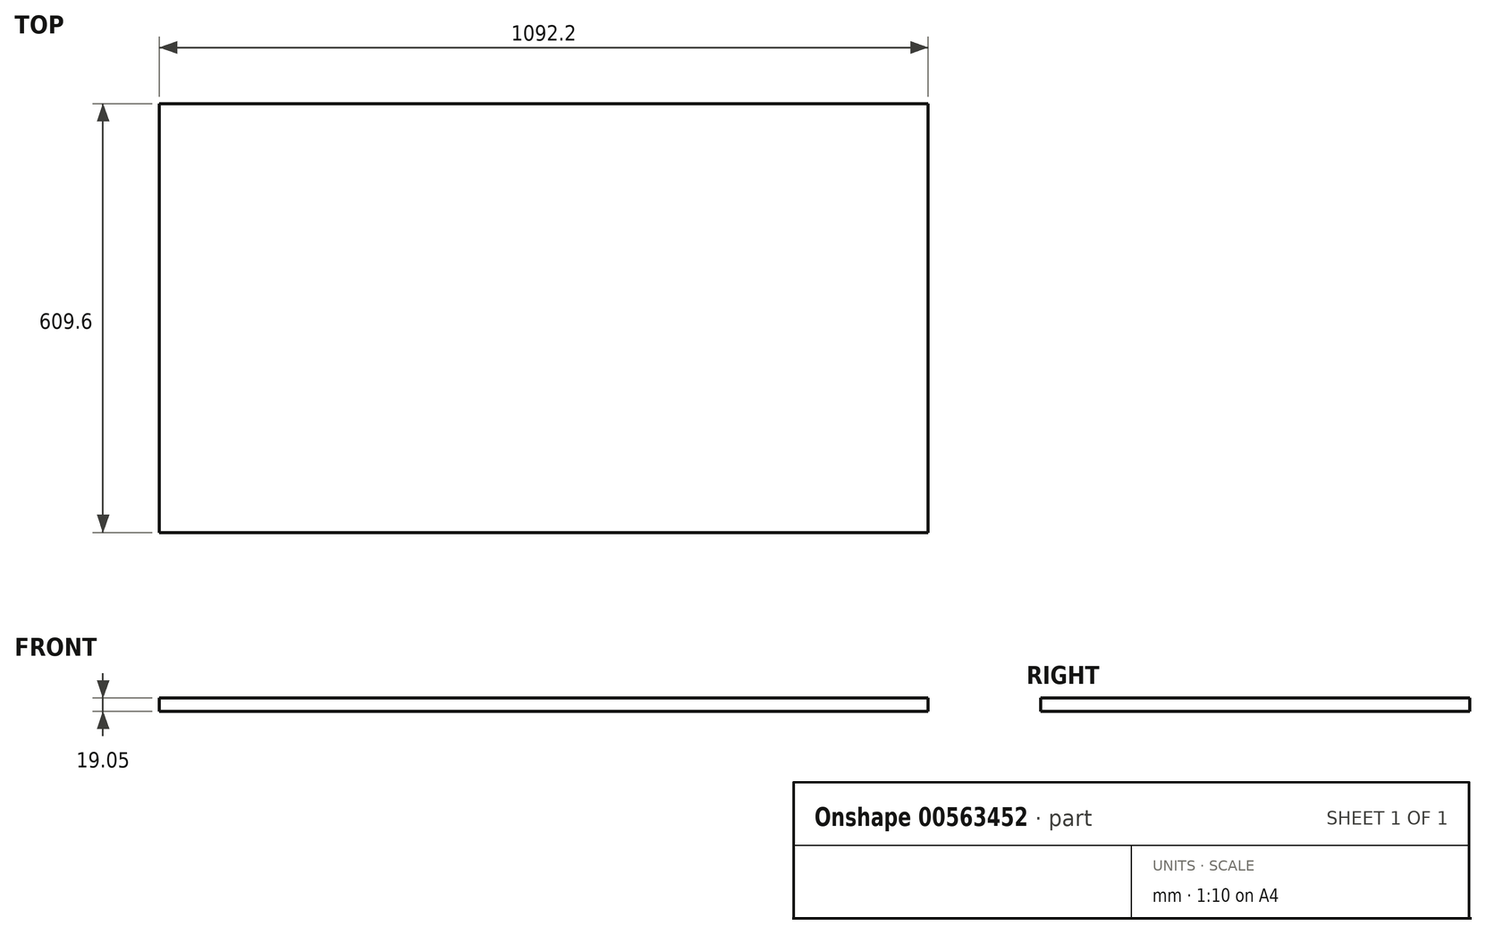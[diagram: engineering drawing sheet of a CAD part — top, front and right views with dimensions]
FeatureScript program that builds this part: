
annotation { "Feature Type Name" : "Feature", "Feature Type Description" : "" }
export const myFeature = defineFeature(function(context is Context, id is Id, definition is map)
    precondition{}
    {
        {
            var Q0;
            Q0=qCreatedBy(makeId("Top.planeOp"),FACE);
            var sketch = newSketch(context, id + "F0", { "sketchPlane" : qUnion([Q0])});
            skLineSegment(sketch, "E0.bottom", {"start": v(-265.33, 488.07) * mm, "end": v(826.87, 488.07) * mm});
            skLineSegment(sketch, "E0.top", {"start": v(-265.33, -121.53) * mm, "end": v(826.87, -121.53) * mm});
            skLineSegment(sketch, "E0.left", {"start": v(-265.33, 488.07) * mm, "end": v(-265.33, -121.53) * mm});
            skLineSegment(sketch, "E0.right", {"start": v(826.87, 488.07) * mm, "end": v(826.87, -121.53) * mm});
            skSolve(sketch);
        }
        {
            var Q0;
            Q0=qSketchRegion(id+"F0",true);
            extrude(context, id + "F1", {"entities" : qUnion([Q0]), "depth" : 19.05 * mm, "offsetDistance" : 25.4 * mm});
        }
    });
